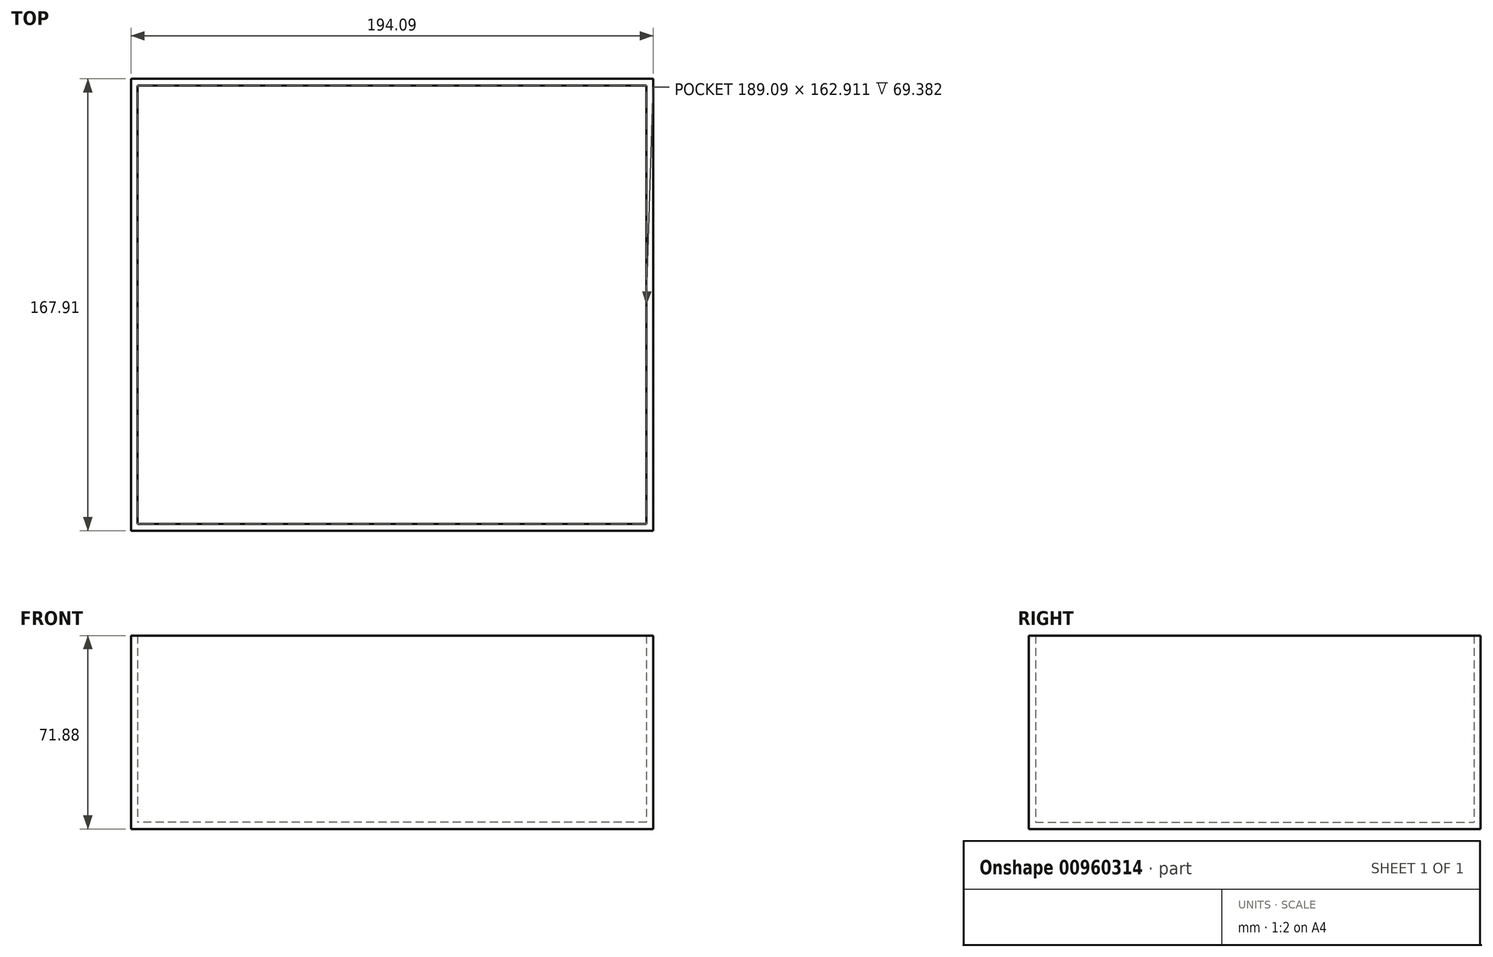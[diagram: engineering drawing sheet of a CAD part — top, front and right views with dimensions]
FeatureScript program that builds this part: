
annotation { "Feature Type Name" : "Feature", "Feature Type Description" : "" }
export const myFeature = defineFeature(function(context is Context, id is Id, definition is map)
    precondition{}
    {
        {
            var Q0;
            Q0=qCreatedBy(makeId("Top.planeOp"),FACE);
            var sketch = newSketch(context, id + "F0", { "sketchPlane" : qUnion([Q0])});
            skLineSegment(sketch, "E0.bottom", {"start": v(72.13, -32.86) * mm, "end": v(-40.96, -32.86) * mm});
            skLineSegment(sketch, "E0.top", {"start": v(72.13, 30.05) * mm, "end": v(-40.96, 30.05) * mm});
            skLineSegment(sketch, "E0.left", {"start": v(72.13, -32.86) * mm, "end": v(72.13, 30.05) * mm});
            skLineSegment(sketch, "E0.right", {"start": v(-40.96, -32.86) * mm, "end": v(-40.96, 30.05) * mm});
            skSolve(sketch);
        }
        {
            var Q0;
            Q0=makeQuery(id+"F0.imprint","IMPRINT",FACE,{"disambiguationData":[TD([[makeQuery(id+"F0.imprint","IMPRINT",EDGE,{"derivedFrom":sQuery(id+"F0.wireOp",EDGE,"E0.bottom")}),-1.0]])]});
            extrude(context, id + "F1", {"entities" : qUnion([Q0]), "depth" : 71.88 * mm, "offsetDistance" : 25.4 * mm});
        }
        {
            var Q0;
            Q0=makeQuery(id+"F1.opExtrude","SWEPT_FACE",FACE,{"disambiguationData":[OSD([sQuery(id+"F0.wireOp",EDGE,"E0.left")])]});
            extrude(context, id + "F2", {"entities" : qUnion([Q0]), "operationType" : NewBodyOperationType.ADD, "depth" : 81 * mm, "offsetDistance" : 25 * mm});
        }
        {
            var Q0;
            {var subQ0=sQuery(id+"F0.wireOp",EDGE,"E0.top");Q0=makeQuery(id+"F2.boolean.opBoolean","MERGE",FACE,{"derivedFrom":[makeQuery(id+"F1.opExtrude","SWEPT_FACE",FACE,{"disambiguationData":[OSD([subQ0])]}),makeQuery(id+"F2.opExtrude","SWEPT_FACE",FACE,{"disambiguationData":[OSD([subQ0,sQuery(id+"F0.wireOp",EDGE,"E0.left")])]})]});}
            extrude(context, id + "F3", {"entities" : qUnion([Q0]), "operationType" : NewBodyOperationType.ADD, "depth" : 105 * mm, "offsetDistance" : 25 * mm});
        }
        {
            var Q0;
            {var subQ0=sQuery(id+"F0.wireOp",EDGE,"E0.left");var subQ1=sQuery(id+"F0.wireOp",EDGE,"E0.top");Q0=makeQuery(id+"F3.boolean.opBoolean","MERGE",FACE,{"derivedFrom":[makeQuery(id+"F2.boolean.opBoolean","MERGE",FACE,{"derivedFrom":[makeQuery(id+"F1.opExtrude","CAP_FACE",FACE,{"disambiguationData":[OSD([sQuery(id+"F0.wireOp",EDGE,"E0.bottom"),subQ1,subQ0,sQuery(id+"F0.wireOp",EDGE,"E0.right")])],"isStart":false}),makeQuery(id+"F2.opExtrude","SWEPT_FACE",FACE,{"disambiguationData":[OSD([subQ0]),TDD([makeQuery(id+"F1.opExtrude","CAP_EDGE",EDGE,{"disambiguationData":[OSD([subQ0])],"isStart":false})])]})]}),makeQuery(id+"F3.opExtrude","SWEPT_FACE",FACE,{"disambiguationData":[OSD([subQ1,subQ0]),TDD([makeQuery(id+"F2.boolean.opBoolean","MERGE",EDGE,{"derivedFrom":[makeQuery(id+"F1.opExtrude","CAP_EDGE",EDGE,{"disambiguationData":[OSD([subQ1])],"isStart":false}),makeQuery(id+"F2.opExtrude","SWEPT_EDGE",EDGE,{"disambiguationData":[OSD([subQ1,subQ0]),TDD([makeQuery(id+"F1.opExtrude","CAP_VERTEX",VERTEX,{"disambiguationData":[OSD([subQ1,subQ0])],"isStart":false})])]})]})])]})]});}
            shell(context, id + "F4", {"entities" : qUnion([Q0]), "thickness" : 2.5 * mm});
        }
    });
